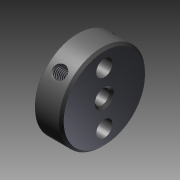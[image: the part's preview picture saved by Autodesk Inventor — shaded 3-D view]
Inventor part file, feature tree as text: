
AUTODESK INVENTOR PART (.ipt)
format: ipt  version: 2015 (Build 190159000, 159)  size: 163,328 bytes
history: native  units: mm
features: sketch x5, revolve x3, thread x2, extrude x2
ambient origin geometry x8: Origin, YZ Plane, XZ Plane, XY Plane, X Axis, Y Axis, Z Axis, Center Point
bodies: Solid1 (feature_tree), body_set_h_XY (feature_tree), body_set_h_YZ (feature_tree), body_set_h_ZX (feature_tree), body_set_h_X (feature_tree), body_set_h_Y (feature_tree), body_set_h_Z (feature_tree), body_set_h_Center (feature_tree), body_set_v_XY (feature_tree), body_set_v_YZ (feature_tree), body_set_v_ZX (feature_tree), body_set_v_X (feature_tree), body_set_v_Y (feature_tree), body_set_v_Z (feature_tree), body_set_v_Center (feature_tree)
feature tree (12):
  revolve  "Revolution1"  Angle=360.0deg
  revolve  "Revolution2"  Angle=360.0deg
  thread  "Thread1"  [1 undecoded]
  revolve  "Revolution3"  [1 undecoded]
  thread  "Thread2"  [1 undecoded]
  extrude  "Extrusion1"  [1 undecoded]
  extrude  "Extrusion2"  [1 undecoded]
  sketch  "Sketch_1"  dims[d0=360.0deg d1=360.0deg]
  sketch  "Sketch_2"  dims[d2=6.959mm d3=0.0mm d4=360.0deg d5=6.959mm d6=0.0mm]
  sketch  "Sketch_3"  dims[d7=12.0mm d8=0.0mm d9=12.0mm d10=0.0mm]
  sketch  "Sketch_6"
  sketch  "Sketch_7"
note: 5 required parameter values undecoded (feature->parameter linkage not recoverable at this tier; creation-order binding heuristic only, values carry confidence <= 0.55)